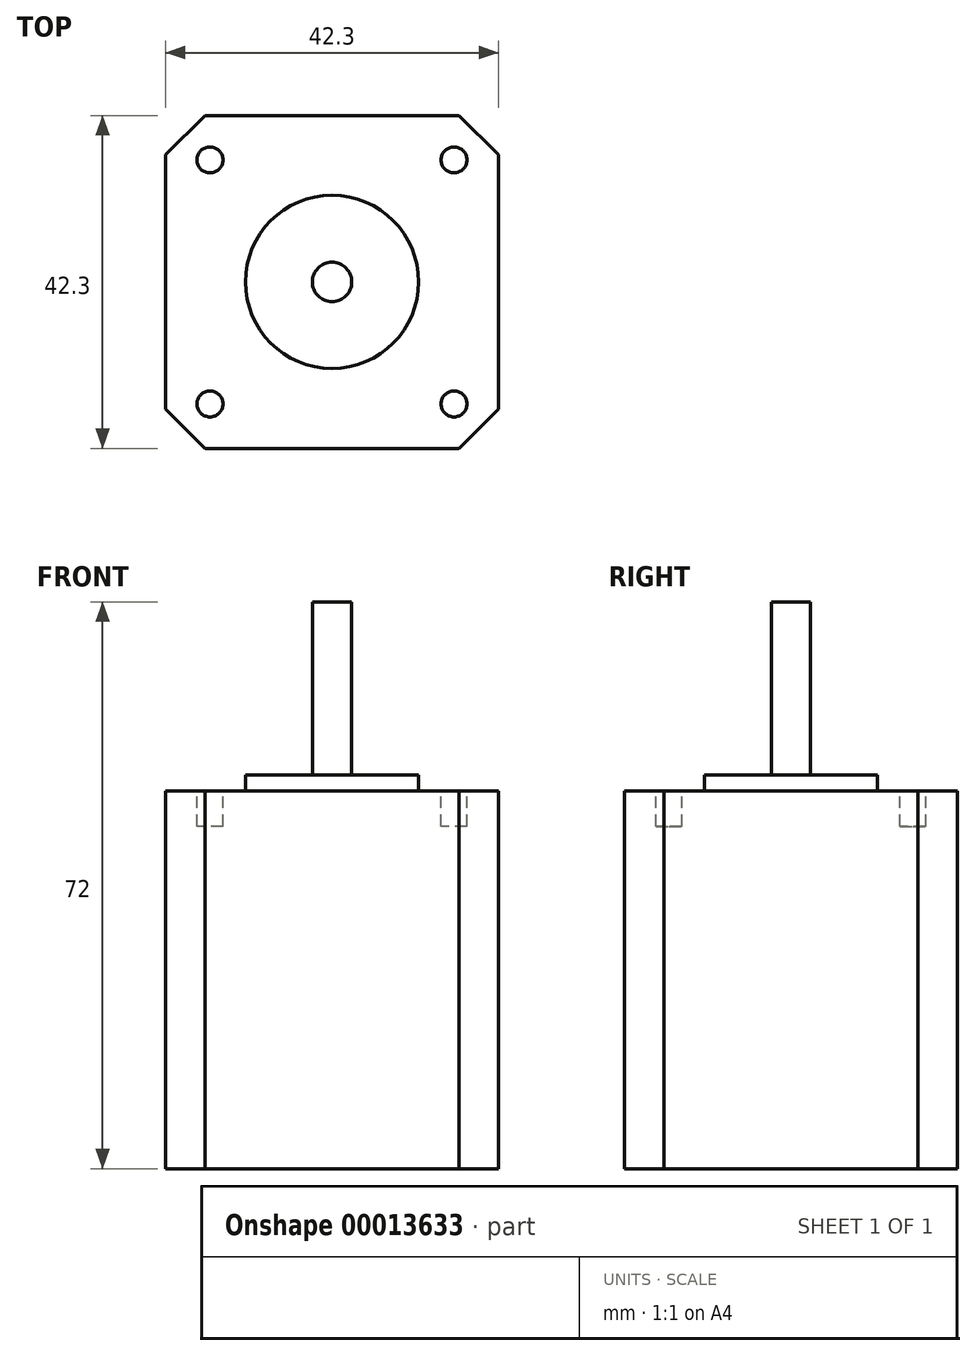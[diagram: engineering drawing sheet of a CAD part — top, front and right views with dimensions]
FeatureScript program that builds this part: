
annotation { "Feature Type Name" : "Feature", "Feature Type Description" : "" }
export const myFeature = defineFeature(function(context is Context, id is Id, definition is map)
    precondition{}
    {
        {
            var Q0;
            Q0=qCreatedBy(makeId("Top.planeOp"),FACE);
            var sketch = newSketch(context, id + "F0", { "sketchPlane" : qUnion([Q0])});
            skLineSegment(sketch, "E0.rect.bottom", {"start": v(21.15, 21.15) * mm, "end": v(-21.15, 21.15) * mm});
            skLineSegment(sketch, "E0.rect.top", {"start": v(21.15, -21.15) * mm, "end": v(-21.15, -21.15) * mm});
            skLineSegment(sketch, "E0.rect.left", {"start": v(21.15, 21.15) * mm, "end": v(21.15, -21.15) * mm});
            skLineSegment(sketch, "E0.rect.right", {"start": v(-21.15, 21.15) * mm, "end": v(-21.15, -21.15) * mm});
            skPoint(sketch, "E0.rect.middle", {"position": v(0, 0) * mm});
            skLineSegment(sketch, "E1.rect.bottom", {"start": v(15.5, 15.5) * mm, "end": v(-15.5, 15.5) * mm, "construction": true});
            skLineSegment(sketch, "E1.rect.top", {"start": v(15.5, -15.5) * mm, "end": v(-15.5, -15.5) * mm, "construction": true});
            skLineSegment(sketch, "E1.rect.left", {"start": v(15.5, 15.5) * mm, "end": v(15.5, -15.5) * mm, "construction": true});
            skLineSegment(sketch, "E1.rect.right", {"start": v(-15.5, 15.5) * mm, "end": v(-15.5, -15.5) * mm, "construction": true});
            skCircle(sketch, "E2", {"center": v(-15.5, -15.5) * mm, "radius": 1.65 * mm});
            skCircle(sketch, "E3", {"center": v(15.5, -15.5) * mm, "radius": 1.65 * mm});
            skCircle(sketch, "E4", {"center": v(15.5, 15.5) * mm, "radius": 1.65 * mm});
            skCircle(sketch, "E5", {"center": v(-15.5, 15.5) * mm, "radius": 1.65 * mm});
            skCircle(sketch, "E6", {"center": v(0, 0) * mm, "radius": 11 * mm});
            skCircle(sketch, "E7", {"center": v(0, 0) * mm, "radius": 2.5 * mm});
            skSolve(sketch);
        }
        {
            var Q0;
            Q0=makeQuery(id+"F0.imprint","IMPRINT",FACE,{"disambiguationData":[TD([[makeQuery(id+"F0.imprint","IMPRINT",EDGE,{"derivedFrom":sQuery(id+"F0.wireOp",EDGE,"E4")}),1.0]])]});
            var Q1;
            Q1=makeQuery(id+"F0.imprint","IMPRINT",FACE,{"disambiguationData":[TD([[makeQuery(id+"F0.imprint","IMPRINT",EDGE,{"derivedFrom":sQuery(id+"F0.wireOp",EDGE,"E5")}),1.0]])]});
            var Q2;
            Q2=makeQuery(id+"F0.imprint","IMPRINT",FACE,{"disambiguationData":[TD([[makeQuery(id+"F0.imprint","IMPRINT",EDGE,{"derivedFrom":sQuery(id+"F0.wireOp",EDGE,"E2")}),1.0]])]});
            var Q3;
            Q3=makeQuery(id+"F0.imprint","IMPRINT",FACE,{"disambiguationData":[TD([[makeQuery(id+"F0.imprint","IMPRINT",EDGE,{"derivedFrom":sQuery(id+"F0.wireOp",EDGE,"E3")}),1.0]])]});
            var Q4;
            Q4=makeQuery(id+"F0.imprint","IMPRINT",FACE,{"disambiguationData":[TD([[makeQuery(id+"F0.imprint","IMPRINT",EDGE,{"derivedFrom":sQuery(id+"F0.wireOp",EDGE,"E0.rect.bottom")}),1.0]])]});
            var Q5;
            Q5=makeQuery(id+"F0.imprint","IMPRINT",FACE,{"disambiguationData":[TD([[makeQuery(id+"F0.imprint","IMPRINT",EDGE,{"derivedFrom":sQuery(id+"F0.wireOp",EDGE,"E6")}),1.0]])]});
            var Q6;
            Q6=makeQuery(id+"F0.imprint","IMPRINT",FACE,{"disambiguationData":[TD([[makeQuery(id+"F0.imprint","IMPRINT",EDGE,{"derivedFrom":sQuery(id+"F0.wireOp",EDGE,"E7")}),1.0]])]});
            extrude(context, id + "F1", {"entities" : qUnion([Q0, Q1, Q2, Q3, Q4, Q5, Q6]), "oppositeDirection" : true, "depth" : 48 * mm});
        }
        {
            var Q0;
            Q0=makeQuery(id+"F0.imprint","IMPRINT",FACE,{"disambiguationData":[TD([[makeQuery(id+"F0.imprint","IMPRINT",EDGE,{"derivedFrom":sQuery(id+"F0.wireOp",EDGE,"E2")}),1.0]])]});
            var Q1;
            Q1=makeQuery(id+"F0.imprint","IMPRINT",FACE,{"disambiguationData":[TD([[makeQuery(id+"F0.imprint","IMPRINT",EDGE,{"derivedFrom":sQuery(id+"F0.wireOp",EDGE,"E5")}),1.0]])]});
            var Q2;
            Q2=makeQuery(id+"F0.imprint","IMPRINT",FACE,{"disambiguationData":[TD([[makeQuery(id+"F0.imprint","IMPRINT",EDGE,{"derivedFrom":sQuery(id+"F0.wireOp",EDGE,"E4")}),1.0]])]});
            var Q3;
            Q3=makeQuery(id+"F0.imprint","IMPRINT",FACE,{"disambiguationData":[TD([[makeQuery(id+"F0.imprint","IMPRINT",EDGE,{"derivedFrom":sQuery(id+"F0.wireOp",EDGE,"E3")}),1.0]])]});
            extrude(context, id + "F2", {"entities" : qUnion([Q0, Q1, Q2, Q3]), "operationType" : NewBodyOperationType.REMOVE, "oppositeDirection" : true, "depth" : 4.5 * mm});
        }
        {
            var Q0;
            Q0=makeQuery(id+"F0.imprint","IMPRINT",FACE,{"disambiguationData":[TD([[makeQuery(id+"F0.imprint","IMPRINT",EDGE,{"derivedFrom":sQuery(id+"F0.wireOp",EDGE,"E6")}),1.0]])]});
            extrude(context, id + "F3", {"entities" : qUnion([Q0]), "operationType" : NewBodyOperationType.ADD, "depth" : 2 * mm});
        }
        {
            var Q0;
            Q0=makeQuery(id+"F0.imprint","IMPRINT",FACE,{"disambiguationData":[TD([[makeQuery(id+"F0.imprint","IMPRINT",EDGE,{"derivedFrom":sQuery(id+"F0.wireOp",EDGE,"E7")}),1.0]])]});
            extrude(context, id + "F4", {"entities" : qUnion([Q0]), "operationType" : NewBodyOperationType.ADD, "depth" : 24 * mm});
        }
        {
            var Q0;
            Q0=makeQuery(id+"F1.opExtrude","SWEPT_EDGE",EDGE,{"disambiguationData":[OSD([sQuery(id+"F0.wireOp",EDGE,"E0.rect.top"),sQuery(id+"F0.wireOp",EDGE,"E0.rect.left")])]});
            var Q1;
            Q1=makeQuery(id+"F1.opExtrude","SWEPT_EDGE",EDGE,{"disambiguationData":[OSD([sQuery(id+"F0.wireOp",EDGE,"E0.rect.bottom"),sQuery(id+"F0.wireOp",EDGE,"E0.rect.left")])]});
            var Q2;
            Q2=makeQuery(id+"F1.opExtrude","SWEPT_EDGE",EDGE,{"disambiguationData":[OSD([sQuery(id+"F0.wireOp",EDGE,"E0.rect.bottom"),sQuery(id+"F0.wireOp",EDGE,"E0.rect.right")])]});
            var Q3;
            Q3=makeQuery(id+"F1.opExtrude","SWEPT_EDGE",EDGE,{"disambiguationData":[OSD([sQuery(id+"F0.wireOp",EDGE,"E0.rect.top"),sQuery(id+"F0.wireOp",EDGE,"E0.rect.right")])]});
            chamfer(context, id + "F5", {"entities" : qUnion([Q0, Q1, Q2, Q3]), "width" : 5 * mm, "tangentPropagation" : true});
        }
    });
